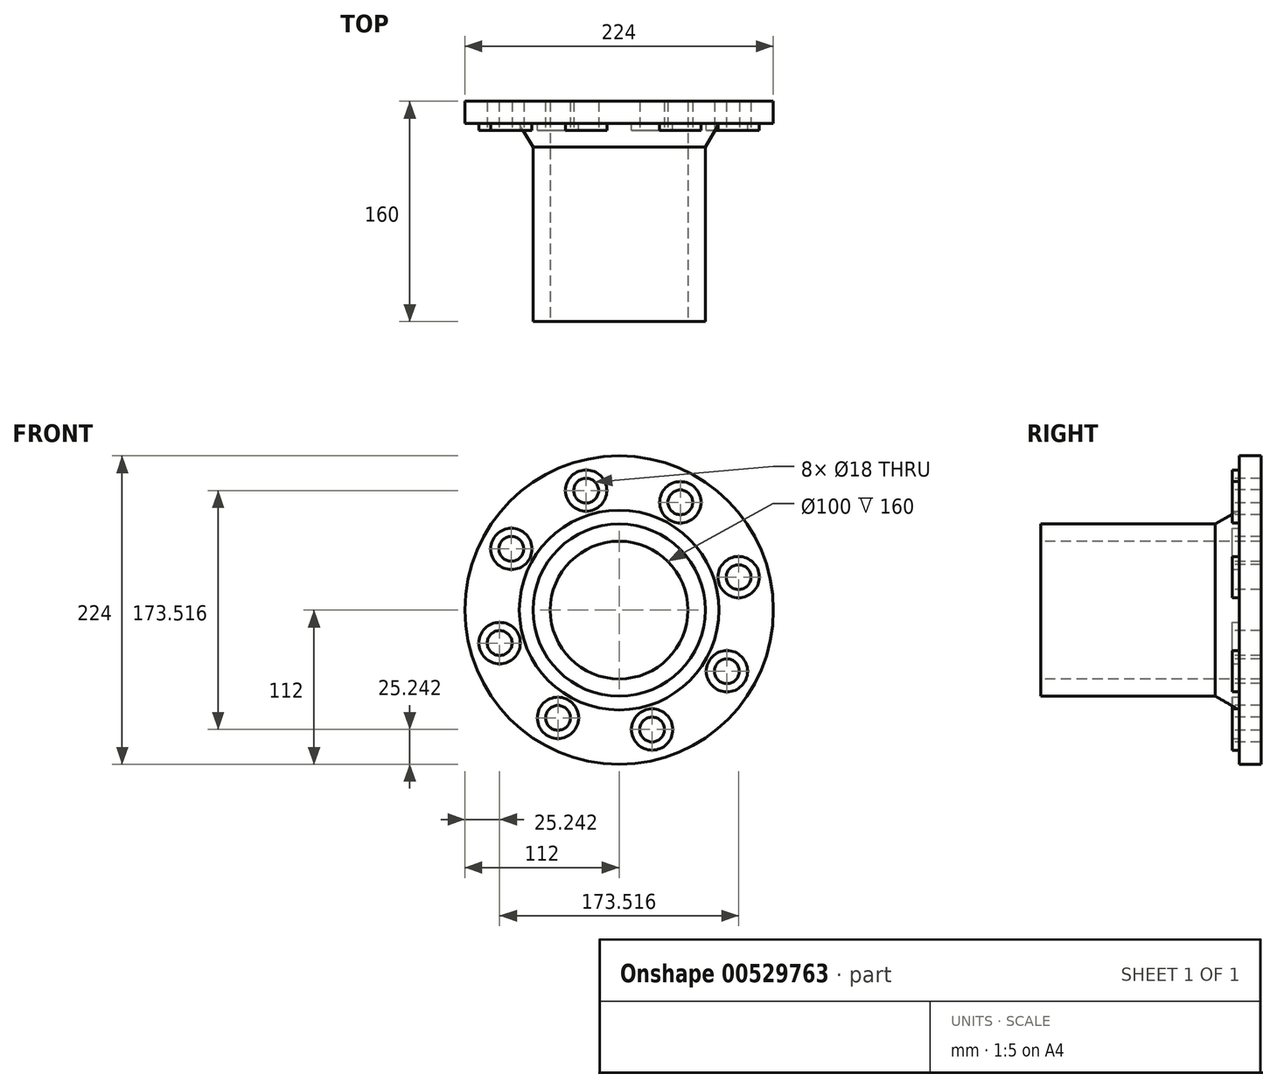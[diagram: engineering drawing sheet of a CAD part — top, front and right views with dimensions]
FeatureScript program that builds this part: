
annotation { "Feature Type Name" : "Feature", "Feature Type Description" : "" }
export const myFeature = defineFeature(function(context is Context, id is Id, definition is map)
    precondition{}
    {
        {
            var Q0;
            Q0=qCreatedBy(makeId("Front.planeOp"),FACE);
            var sketch = newSketch(context, id + "F0", { "sketchPlane" : qUnion([Q0])});
            skCircle(sketch, "E0", {"center": v(0, 0) * mm, "radius": 112 * mm});
            skSolve(sketch);
        }
        {
            var Q0;
            Q0=makeQuery(id+"F0.imprint","IMPRINT",FACE,{"disambiguationData":[TD([[makeQuery(id+"F0.imprint","IMPRINT",EDGE,{"derivedFrom":sQuery(id+"F0.wireOp",EDGE,"E0")}),1.0]])]});
            extrude(context, id + "F1", {"entities" : qUnion([Q0]), "depth" : 16 * mm, "offsetDistance" : 25 * mm});
        }
        {
            var Q0;
            Q0=qCreatedBy(makeId("Front.planeOp"),FACE);
            var sketch = newSketch(context, id + "F2", { "sketchPlane" : qUnion([Q0])});
            skCircle(sketch, "E1", {"center": v(0, 0) * mm, "radius": 62.5 * mm});
            skSolve(sketch);
        }
        {
            var Q0;
            Q0 = qSketchRegion(id + "F2", true);
            extrude(context, id + "F3", {"entities" : qUnion([Q0]), "operationType" : NewBodyOperationType.ADD, "depth" : 160 * mm, "offsetDistance" : 25 * mm});
        }
        {
            var Q0;
            Q0=makeQuery(id+"F3.opExtrude","CAP_FACE",FACE,{"disambiguationData":[OSD([sQuery(id+"F2.wireOp",EDGE,"E1")])],"isStart":false});
            var sketch = newSketch(context, id + "F4", { "sketchPlane" : qUnion([Q0])});
            skCircle(sketch, "E2", {"center": v(0, 0) * mm, "radius": 50 * mm});
            skSolve(sketch);
        }
        {
            var Q0;
            Q0=makeQuery(id+"F4.imprint","IMPRINT",FACE,{"disambiguationData":[TD([[makeQuery(id+"F4.imprint","IMPRINT",EDGE,{"derivedFrom":sQuery(id+"F4.wireOp",EDGE,"E2")}),1.0]])]});
            extrude(context, id + "F5", {"entities" : qUnion([Q0]), "operationType" : NewBodyOperationType.REMOVE, "endBound" : BoundingType.THROUGH_ALL, "oppositeDirection" : true, "depth" : 25 * mm, "offsetDistance" : 25 * mm});
        }
        {
            var Q0;
            Q0=makeQuery(id+"F1.opExtrude","CAP_FACE",FACE,{"disambiguationData":[OSD([sQuery(id+"F0.wireOp",EDGE,"E0")])],"isStart":false});
            var sketch = newSketch(context, id + "F6", { "sketchPlane" : qUnion([Q0])});
            skCircle(sketch, "E3", {"center": v(0, 0) * mm, "radius": 90 * mm, "construction": true});
            skCircle(sketch, "E4", {"center": v(-78.27, 44.42) * mm, "radius": 9 * mm});
            skCircle(sketch, "E5.1.0", {"center": v(-86.76, -23.94) * mm, "radius": 9 * mm});
            skCircle(sketch, "E5.2.0", {"center": v(-44.42, -78.27) * mm, "radius": 9 * mm});
            skCircle(sketch, "E5.3.0", {"center": v(23.94, -86.76) * mm, "radius": 9 * mm});
            skCircle(sketch, "E5.4.0", {"center": v(78.27, -44.42) * mm, "radius": 9 * mm});
            skCircle(sketch, "E5.5.0", {"center": v(86.76, 23.94) * mm, "radius": 9 * mm});
            skCircle(sketch, "E5.6.0", {"center": v(44.42, 78.27) * mm, "radius": 9 * mm});
            skCircle(sketch, "E5.7.0", {"center": v(-23.94, 86.76) * mm, "radius": 9 * mm});
            skSolve(sketch);
        }
        {
            var Q0;
            Q0 = qSketchRegion(id + "F6", true);
            extrude(context, id + "F7", {"entities" : qUnion([Q0]), "operationType" : NewBodyOperationType.REMOVE, "endBound" : BoundingType.THROUGH_ALL, "oppositeDirection" : true, "depth" : 25 * mm, "offsetDistance" : 25 * mm});
        }
        {
            var Q0;
            Q0=makeQuery(id+"F1.opExtrude","CAP_FACE",FACE,{"disambiguationData":[OSD([sQuery(id+"F0.wireOp",EDGE,"E0")])],"isStart":false});
            var sketch = newSketch(context, id + "F8", { "sketchPlane" : qUnion([Q0])});
            skCircle(sketch, "E6", {"center": v(0, 0) * mm, "radius": 90 * mm, "construction": true});
            skCircle(sketch, "E7", {"center": v(44.42, 78.27) * mm, "radius": 15 * mm});
            skCircle(sketch, "E8.1.0", {"center": v(-23.94, 86.76) * mm, "radius": 15 * mm});
            skCircle(sketch, "E8.2.0", {"center": v(-78.27, 44.42) * mm, "radius": 15 * mm});
            skCircle(sketch, "E8.3.0", {"center": v(-86.76, -23.94) * mm, "radius": 15 * mm});
            skCircle(sketch, "E8.4.0", {"center": v(-44.42, -78.27) * mm, "radius": 15 * mm});
            skCircle(sketch, "E8.5.0", {"center": v(23.94, -86.76) * mm, "radius": 15 * mm});
            skCircle(sketch, "E8.6.0", {"center": v(78.27, -44.42) * mm, "radius": 15 * mm});
            skCircle(sketch, "E8.7.0", {"center": v(86.76, 23.94) * mm, "radius": 15 * mm});
            skSolve(sketch);
        }
        {
            var Q0;
            Q0=makeQuery(id+"F8.imprint","IMPRINT",FACE,{"disambiguationData":[TD([[makeQuery(id+"F8.imprint","IMPRINT",EDGE,{"derivedFrom":sQuery(id+"F8.wireOp",EDGE,"E7")}),1.0]])]});
            var Q1;
            Q1=makeQuery(id+"F8.imprint","IMPRINT",FACE,{"disambiguationData":[TD([[makeQuery(id+"F8.imprint","IMPRINT",EDGE,{"derivedFrom":sQuery(id+"F8.wireOp",EDGE,"E8.7.0")}),1.0]])]});
            var Q2;
            Q2=makeQuery(id+"F8.imprint","IMPRINT",FACE,{"disambiguationData":[TD([[makeQuery(id+"F8.imprint","IMPRINT",EDGE,{"derivedFrom":sQuery(id+"F8.wireOp",EDGE,"E8.6.0")}),1.0]])]});
            var Q3;
            Q3=makeQuery(id+"F8.imprint","IMPRINT",FACE,{"disambiguationData":[TD([[makeQuery(id+"F8.imprint","IMPRINT",EDGE,{"derivedFrom":sQuery(id+"F8.wireOp",EDGE,"E8.5.0")}),1.0]])]});
            var Q4;
            Q4=makeQuery(id+"F8.imprint","IMPRINT",FACE,{"disambiguationData":[TD([[makeQuery(id+"F8.imprint","IMPRINT",EDGE,{"derivedFrom":sQuery(id+"F8.wireOp",EDGE,"E8.4.0")}),1.0]])]});
            var Q5;
            Q5=makeQuery(id+"F8.imprint","IMPRINT",FACE,{"disambiguationData":[TD([[makeQuery(id+"F8.imprint","IMPRINT",EDGE,{"derivedFrom":sQuery(id+"F8.wireOp",EDGE,"E8.3.0")}),1.0]])]});
            var Q6;
            Q6=makeQuery(id+"F8.imprint","IMPRINT",FACE,{"disambiguationData":[TD([[makeQuery(id+"F8.imprint","IMPRINT",EDGE,{"derivedFrom":sQuery(id+"F8.wireOp",EDGE,"E8.2.0")}),1.0]])]});
            var Q7;
            Q7=makeQuery(id+"F8.imprint","IMPRINT",FACE,{"disambiguationData":[TD([[makeQuery(id+"F8.imprint","IMPRINT",EDGE,{"derivedFrom":sQuery(id+"F8.wireOp",EDGE,"E8.1.0")}),1.0]])]});
            extrude(context, id + "F9", {"entities" : qUnion([Q0, Q1, Q2, Q3, Q4, Q5, Q6, Q7]), "operationType" : NewBodyOperationType.ADD, "depth" : 5 * mm, "offsetDistance" : 25 * mm});
        }
        {
            var Q0;
            Q0=makeQuery(id+"F3.boolean.opBoolean","INTERSECT",EDGE,{"derivedFrom":[makeQuery(id+"F1.opExtrude","CAP_FACE",FACE,{"disambiguationData":[OSD([sQuery(id+"F0.wireOp",EDGE,"E0")])],"isStart":false}),makeQuery(id+"F3.opExtrude","SWEPT_FACE",FACE,{"disambiguationData":[OSD([sQuery(id+"F2.wireOp",EDGE,"E1")])]})]});
            chamfer(context, id + "F10", {"entities" : qUnion([Q0]), "chamferType" : ChamferType.OFFSET_ANGLE, "width" : 10 * mm, "oppositeDirection" : false, "angle" : 60 * degree, "tangentPropagation" : true});
        }
    });
